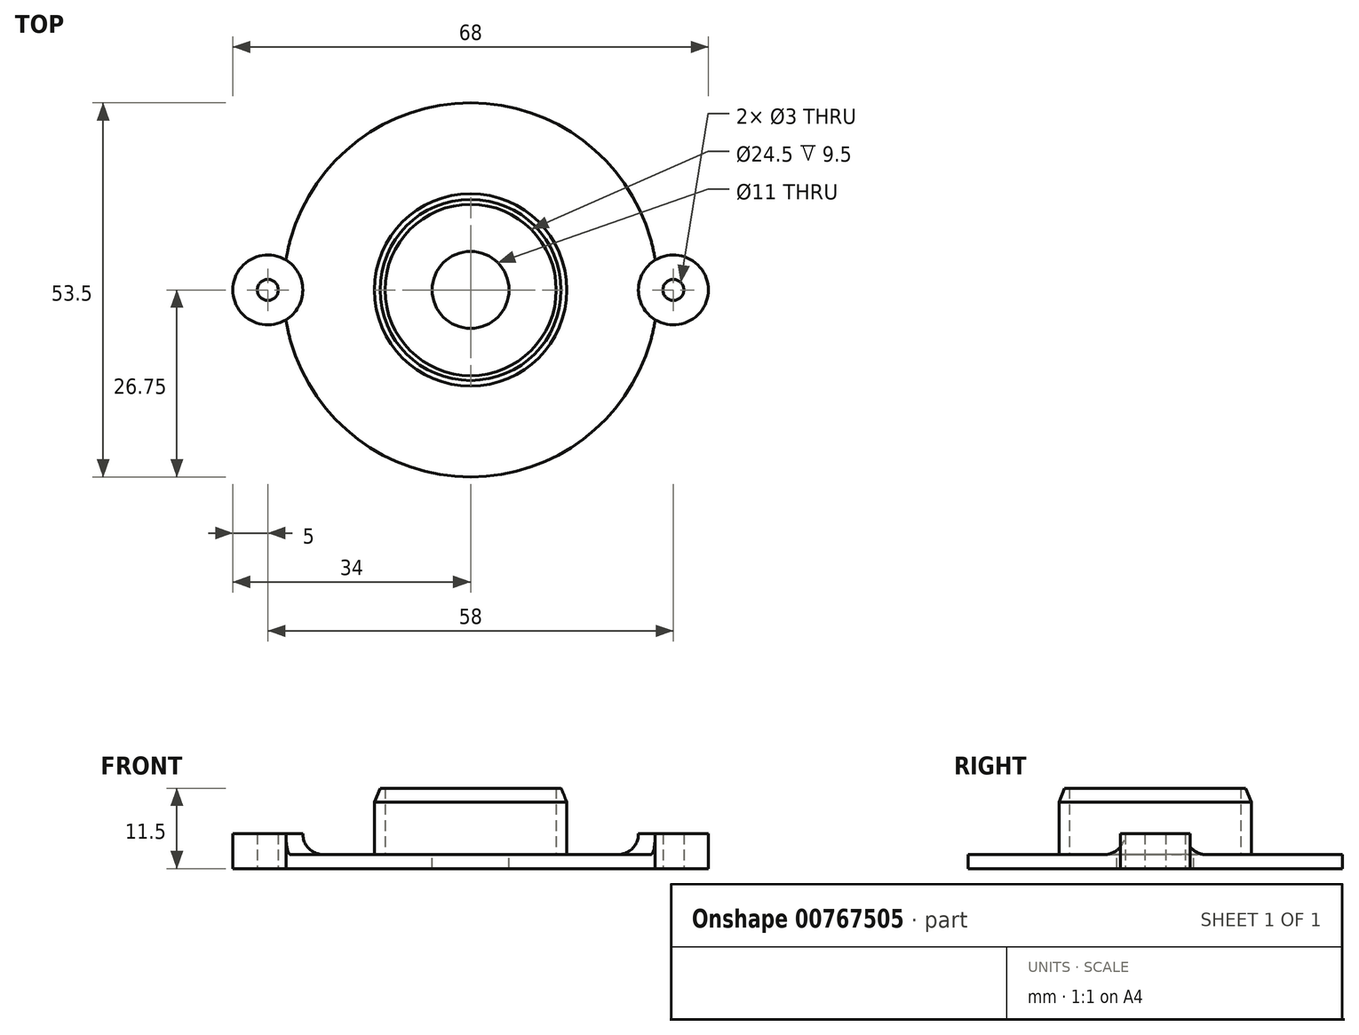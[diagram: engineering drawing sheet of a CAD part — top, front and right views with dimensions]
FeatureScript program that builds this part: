
annotation { "Feature Type Name" : "Feature", "Feature Type Description" : "" }
export const myFeature = defineFeature(function(context is Context, id is Id, definition is map)
    precondition{}
    {
        {
            var Q0;
            Q0=qCreatedBy(makeId("Top.planeOp"),FACE);
            var sketch = newSketch(context, id + "F0", { "sketchPlane" : qUnion([Q0])});
            skCircle(sketch, "E0", {"center": v(0, 0) * mm, "radius": 26.75 * mm});
            skSolve(sketch);
        }
        {
            var Q0;
            Q0=makeQuery(id+"F0.imprint","IMPRINT",FACE,{"disambiguationData":[TD([[makeQuery(id+"F0.imprint","IMPRINT",EDGE,{"derivedFrom":sQuery(id+"F0.wireOp",EDGE,"E0")}),1.0]])]});
            extrude(context, id + "F1", {"entities" : qUnion([Q0]), "depth" : 2 * mm, "offsetDistance" : 25 * mm});
        }
        {
            var Q0;
            Q0=makeQuery(id+"F1.opExtrude","CAP_FACE",FACE,{"disambiguationData":[OSD([sQuery(id+"F0.wireOp",EDGE,"E0")])],"isStart":false});
            var sketch = newSketch(context, id + "F2", { "sketchPlane" : qUnion([Q0])});
            skCircle(sketch, "E1", {"center": v(0, 0) * mm, "radius": 12.25 * mm});
            skCircle(sketch, "E2", {"center": v(0, 0) * mm, "radius": 13.75 * mm});
            skSolve(sketch);
        }
        {
            var Q0;
            Q0=makeQuery(id+"F2.imprint","IMPRINT",FACE,{"disambiguationData":[TD([[makeQuery(id+"F2.imprint","IMPRINT",EDGE,{"derivedFrom":sQuery(id+"F2.wireOp",EDGE,"E1")}),-1.0]])]});
            extrude(context, id + "F3", {"entities" : qUnion([Q0]), "operationType" : NewBodyOperationType.ADD, "depth" : 9.5 * mm, "offsetDistance" : 25 * mm});
        }
        {
            var Q0;
            Q0=makeQuery(id+"F3.opExtrude","CAP_EDGE",EDGE,{"disambiguationData":[OSD([sQuery(id+"F2.wireOp",EDGE,"E2")])],"isStart":false});
            chamfer(context, id + "F4", {"entities" : qUnion([Q0]), "chamferType" : ChamferType.TWO_OFFSETS, "width1" : 0.8 * mm, "oppositeDirection" : false, "width2" : 2 * mm, "tangentPropagation" : true});
        }
        {
            var Q0;
            Q0=makeQuery(id+"F1.opExtrude","CAP_FACE",FACE,{"disambiguationData":[OSD([sQuery(id+"F0.wireOp",EDGE,"E0")])],"isStart":false});
            var sketch = newSketch(context, id + "F5", { "sketchPlane" : qUnion([Q0])});
            skCircle(sketch, "E3", {"center": v(0, 0) * mm, "radius": 5.5 * mm});
            skSolve(sketch);
        }
        {
            var Q0;
            Q0=makeQuery(id+"F5.imprint","IMPRINT",FACE,{"disambiguationData":[TD([[makeQuery(id+"F5.imprint","IMPRINT",EDGE,{"derivedFrom":sQuery(id+"F5.wireOp",EDGE,"E3")}),1.0]])]});
            extrude(context, id + "F6", {"entities" : qUnion([Q0]), "operationType" : NewBodyOperationType.REMOVE, "oppositeDirection" : true, "depth" : 25 * mm, "offsetDistance" : 25 * mm});
        }
        {
            var Q0;
            Q0=qCreatedBy(makeId("Top.planeOp"),FACE);
            var sketch = newSketch(context, id + "F7", { "sketchPlane" : qUnion([Q0])});
            skCircle(sketch, "E4", {"center": v(29, 0) * mm, "radius": 5 * mm});
            skCircle(sketch, "E5", {"center": v(29, 0) * mm, "radius": 1.5 * mm});
            skCircle(sketch, "E6.1.0", {"center": v(-29, 0) * mm, "radius": 1.5 * mm});
            skCircle(sketch, "E6.1.1", {"center": v(-29, 0) * mm, "radius": 5 * mm});
            skPoint(sketch, "E6.center", {"position": v(0, 0) * mm});
            skSolve(sketch);
        }
        {
            var Q0;
            Q0=makeQuery(id+"F7.imprint","IMPRINT",FACE,{"disambiguationData":[TD([[makeQuery(id+"F7.imprint","IMPRINT",EDGE,{"derivedFrom":sQuery(id+"F7.wireOp",EDGE,"E6.1.0")}),-1.0]])]});
            var Q1;
            Q1=makeQuery(id+"F7.imprint","IMPRINT",FACE,{"disambiguationData":[TD([[makeQuery(id+"F7.imprint","IMPRINT",EDGE,{"derivedFrom":sQuery(id+"F7.wireOp",EDGE,"E4")}),1.0]])]});
            extrude(context, id + "F8", {"entities" : qUnion([Q0, Q1]), "operationType" : NewBodyOperationType.ADD, "depth" : 5 * mm, "offsetDistance" : 25 * mm});
        }
        {
            var Q0;
            {var subQ0=sQuery(id+"F0.wireOp",EDGE,"E0");Q0=makeQuery(id+"F8.boolean.opBoolean","INTERSECT",EDGE,{"derivedFrom":[makeQuery(id+"F3.boolean.opBoolean","SPLIT",FACE,{"disambiguationData":[TD([makeQuery(id+"F1.opExtrude","SWEPT_FACE",FACE,{"disambiguationData":[OSD([subQ0])]})])],"derivedFrom":makeQuery(id+"F1.opExtrude","CAP_FACE",FACE,{"disambiguationData":[OSD([subQ0])],"isStart":false})}),makeQuery(id+"F8.opExtrude","SWEPT_FACE",FACE,{"disambiguationData":[OSD([sQuery(id+"F7.wireOp",EDGE,"E6.1.1")])]})]});}
            var Q1;
            {var subQ0=sQuery(id+"F0.wireOp",EDGE,"E0");Q1=makeQuery(id+"F8.boolean.opBoolean","INTERSECT",EDGE,{"derivedFrom":[makeQuery(id+"F3.boolean.opBoolean","SPLIT",FACE,{"disambiguationData":[TD([makeQuery(id+"F1.opExtrude","SWEPT_FACE",FACE,{"disambiguationData":[OSD([subQ0])]})])],"derivedFrom":makeQuery(id+"F1.opExtrude","CAP_FACE",FACE,{"disambiguationData":[OSD([subQ0])],"isStart":false})}),makeQuery(id+"F8.opExtrude","SWEPT_FACE",FACE,{"disambiguationData":[OSD([sQuery(id+"F7.wireOp",EDGE,"E4")])]})]});}
            fillet(context, id + "F9", {"entities" : qUnion([Q0, Q1]), "radius" : 3 * mm, "tangentPropagation" : true, "allowEdgeOverflow" : false});
        }
    });
